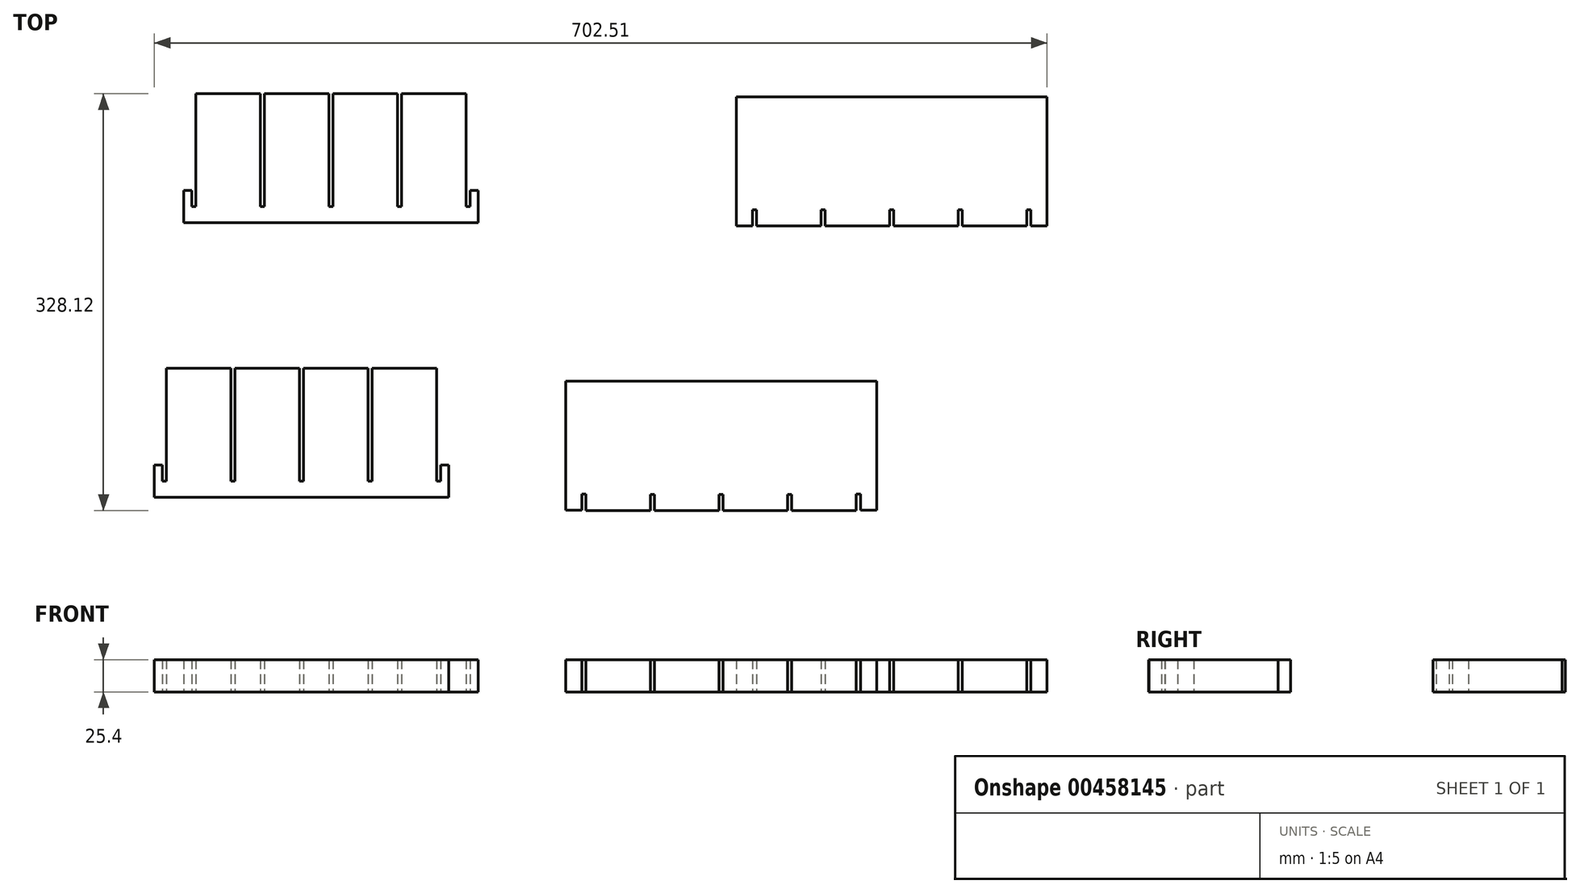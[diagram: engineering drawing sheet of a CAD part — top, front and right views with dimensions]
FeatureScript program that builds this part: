
annotation { "Feature Type Name" : "Feature", "Feature Type Description" : "" }
export const myFeature = defineFeature(function(context is Context, id is Id, definition is map)
    precondition{}
    {
        {
            var Q0;
            Q0=qCreatedBy(makeId("Top.planeOp"),FACE);
            var sketch = newSketch(context, id + "F0", { "sketchPlane" : qUnion([Q0])});
            skLineSegment(sketch, "E0", {"start": v(-688.87, 490.39) * mm, "end": v(-476.15, 490.39) * mm});
            skLineSegment(sketch, "E1", {"start": v(-476.15, 503.09) * mm, "end": v(-476.15, 591.99) * mm});
            skLineSegment(sketch, "E2", {"start": v(-476.15, 591.99) * mm, "end": v(-526.95, 591.99) * mm});
            skLineSegment(sketch, "E3", {"start": v(-526.95, 591.99) * mm, "end": v(-526.95, 503.09) * mm});
            skLineSegment(sketch, "E4", {"start": v(-530.12, 503.09) * mm, "end": v(-530.12, 591.99) * mm});
            skLineSegment(sketch, "E5", {"start": v(-530.12, 591.99) * mm, "end": v(-580.92, 591.99) * mm});
            skLineSegment(sketch, "E6", {"start": v(-580.92, 591.99) * mm, "end": v(-580.92, 503.09) * mm});
            skLineSegment(sketch, "E7", {"start": v(-584.1, 503.09) * mm, "end": v(-584.1, 591.99) * mm});
            skLineSegment(sketch, "E8", {"start": v(-584.1, 591.99) * mm, "end": v(-634.9, 591.99) * mm});
            skLineSegment(sketch, "E9", {"start": v(-634.9, 591.99) * mm, "end": v(-634.9, 503.09) * mm});
            skLineSegment(sketch, "E10", {"start": v(-638.07, 503.09) * mm, "end": v(-638.07, 591.99) * mm});
            skLineSegment(sketch, "E11", {"start": v(-638.07, 591.99) * mm, "end": v(-688.87, 591.99) * mm});
            skLineSegment(sketch, "E12", {"start": v(-688.87, 591.99) * mm, "end": v(-688.87, 503.09) * mm});
            skLineSegment(sketch, "E13", {"start": v(-584.1, 503.09) * mm, "end": v(-580.92, 503.09) * mm});
            skLineSegment(sketch, "E14", {"start": v(-530.12, 503.09) * mm, "end": v(-526.95, 503.09) * mm});
            skLineSegment(sketch, "E15", {"start": v(-638.07, 503.09) * mm, "end": v(-634.9, 503.09) * mm});
            skPoint(sketch, "E16.orphan", {"position": v(-526.95, 490.39) * mm});
            skPoint(sketch, "E17.start.orphan", {"position": v(-526.78, 490.39) * mm});
            skPoint(sketch, "E18.start.orphan", {"position": v(-580.92, 490.39) * mm});
            skPoint(sketch, "E19.start.orphan", {"position": v(-634.9, 490.39) * mm});
            skLineSegment(sketch, "E20.bottom", {"start": v(-688.87, 490.39) * mm, "end": v(-698.4, 490.39) * mm});
            skLineSegment(sketch, "E20.top", {"start": v(-688.87, 503.09) * mm, "end": v(-692.05, 503.09) * mm});
            skLineSegment(sketch, "E21.bottom", {"start": v(-476.15, 490.39) * mm, "end": v(-466.62, 490.39) * mm});
            skLineSegment(sketch, "E22", {"start": v(-247.78, 487.8) * mm, "end": v(-196.98, 487.8) * mm});
            skLineSegment(sketch, "E23", {"start": v(-247.78, 500.5) * mm, "end": v(-247.78, 487.8) * mm});
            skLineSegment(sketch, "E24", {"start": v(-143, 500.5) * mm, "end": v(-139.83, 500.5) * mm});
            skLineSegment(sketch, "E25", {"start": v(-89.03, 500.5) * mm, "end": v(-85.86, 500.5) * mm});
            skLineSegment(sketch, "E26", {"start": v(-196.98, 500.5) * mm, "end": v(-193.8, 500.5) * mm});
            skPoint(sketch, "E27.orphan", {"position": v(-85.86, 487.8) * mm});
            skPoint(sketch, "E28.start.orphan", {"position": v(-139.83, 487.8) * mm});
            skPoint(sketch, "E29.start.orphan", {"position": v(-193.8, 487.8) * mm});
            skLineSegment(sketch, "E30", {"start": v(-193.8, 500.5) * mm, "end": v(-193.8, 487.8) * mm});
            skLineSegment(sketch, "E31", {"start": v(-196.98, 500.5) * mm, "end": v(-196.98, 487.8) * mm});
            skLineSegment(sketch, "E32", {"start": v(-143, 500.5) * mm, "end": v(-143, 487.8) * mm});
            skLineSegment(sketch, "E33", {"start": v(-139.83, 500.5) * mm, "end": v(-139.83, 487.8) * mm});
            skLineSegment(sketch, "E34", {"start": v(-89.03, 500.5) * mm, "end": v(-89.03, 487.8) * mm});
            skLineSegment(sketch, "E35", {"start": v(-85.86, 500.5) * mm, "end": v(-85.86, 487.8) * mm});
            skLineSegment(sketch, "E36.trimOffspring", {"start": v(-193.8, 487.8) * mm, "end": v(-143, 487.8) * mm});
            skLineSegment(sketch, "E37.trimOffspring", {"start": v(-139.83, 487.8) * mm, "end": v(-89.03, 487.8) * mm});
            skLineSegment(sketch, "E38.trimOffspring", {"start": v(-85.86, 487.8) * mm, "end": v(-35.06, 487.8) * mm});
            skLineSegment(sketch, "E39", {"start": v(-263.66, 589.4) * mm, "end": v(-19.06, 589.4) * mm});
            skLineSegment(sketch, "E40.top", {"start": v(-247.78, 500.5) * mm, "end": v(-250.96, 500.5) * mm});
            skLineSegment(sketch, "E41.top", {"start": v(-35.06, 500.5) * mm, "end": v(-31.76, 500.5) * mm});
            skLineSegment(sketch, "E42.top", {"start": v(-31.76, 487.8) * mm, "end": v(-19.06, 487.8) * mm});
            skLineSegment(sketch, "E42.left", {"start": v(-31.76, 500.5) * mm, "end": v(-31.76, 487.8) * mm});
            skLineSegment(sketch, "E42.right", {"start": v(-19.06, 589.4) * mm, "end": v(-19.06, 487.8) * mm});
            skLineSegment(sketch, "E43.top", {"start": v(-250.96, 487.8) * mm, "end": v(-263.66, 487.8) * mm});
            skLineSegment(sketch, "E43.left", {"start": v(-250.96, 500.5) * mm, "end": v(-250.96, 487.8) * mm});
            skLineSegment(sketch, "E43.right", {"start": v(-263.66, 589.4) * mm, "end": v(-263.66, 487.8) * mm});
            skLineSegment(sketch, "E44", {"start": v(-35.06, 500.5) * mm, "end": v(-35.06, 487.8) * mm});
            skLineSegment(sketch, "E45", {"start": v(-381.95, 263.87) * mm, "end": v(-331.15, 263.87) * mm});
            skLineSegment(sketch, "E46", {"start": v(-381.95, 276.9) * mm, "end": v(-381.95, 263.87) * mm});
            skLineSegment(sketch, "E47", {"start": v(-277.18, 276.57) * mm, "end": v(-274, 276.57) * mm});
            skLineSegment(sketch, "E48", {"start": v(-223.2, 276.57) * mm, "end": v(-220.03, 276.57) * mm});
            skLineSegment(sketch, "E49", {"start": v(-331.15, 276.57) * mm, "end": v(-327.98, 276.57) * mm});
            skPoint(sketch, "E50.orphan", {"position": v(-220.03, 263.87) * mm});
            skPoint(sketch, "E51.start.orphan", {"position": v(-274, 263.87) * mm});
            skPoint(sketch, "E52.start.orphan", {"position": v(-327.98, 263.87) * mm});
            skLineSegment(sketch, "E53", {"start": v(-327.98, 276.57) * mm, "end": v(-327.98, 263.87) * mm});
            skLineSegment(sketch, "E54", {"start": v(-331.15, 276.57) * mm, "end": v(-331.15, 263.87) * mm});
            skLineSegment(sketch, "E55", {"start": v(-277.18, 276.57) * mm, "end": v(-277.18, 263.87) * mm});
            skLineSegment(sketch, "E56", {"start": v(-274, 276.57) * mm, "end": v(-274, 263.87) * mm});
            skLineSegment(sketch, "E57", {"start": v(-223.2, 276.57) * mm, "end": v(-223.2, 263.87) * mm});
            skLineSegment(sketch, "E58", {"start": v(-220.03, 276.57) * mm, "end": v(-220.03, 263.87) * mm});
            skLineSegment(sketch, "E59.trimOffspring", {"start": v(-327.98, 263.87) * mm, "end": v(-277.18, 263.87) * mm});
            skLineSegment(sketch, "E60.trimOffspring", {"start": v(-274, 263.87) * mm, "end": v(-223.2, 263.87) * mm});
            skLineSegment(sketch, "E61.trimOffspring", {"start": v(-220.03, 263.87) * mm, "end": v(-169.23, 263.87) * mm});
            skLineSegment(sketch, "E62", {"start": v(-397.83, 365.8) * mm, "end": v(-153.22, 365.8) * mm});
            skLineSegment(sketch, "E63.top", {"start": v(-381.95, 276.9) * mm, "end": v(-385.13, 276.9) * mm});
            skLineSegment(sketch, "E64.top", {"start": v(-169.23, 276.9) * mm, "end": v(-165.92, 276.9) * mm});
            skLineSegment(sketch, "E65.top", {"start": v(-165.92, 264.2) * mm, "end": v(-153.22, 264.2) * mm});
            skLineSegment(sketch, "E65.left", {"start": v(-165.92, 276.9) * mm, "end": v(-165.92, 264.2) * mm});
            skLineSegment(sketch, "E65.right", {"start": v(-153.22, 365.8) * mm, "end": v(-153.22, 264.2) * mm});
            skLineSegment(sketch, "E66.top", {"start": v(-385.13, 264.2) * mm, "end": v(-397.83, 264.2) * mm});
            skLineSegment(sketch, "E66.left", {"start": v(-385.13, 276.9) * mm, "end": v(-385.13, 264.2) * mm});
            skLineSegment(sketch, "E66.right", {"start": v(-397.83, 365.8) * mm, "end": v(-397.83, 264.2) * mm});
            skLineSegment(sketch, "E67", {"start": v(-169.23, 276.9) * mm, "end": v(-169.23, 263.87) * mm});
            skLineSegment(sketch, "E68", {"start": v(-476.15, 503.09) * mm, "end": v(-472.97, 503.09) * mm});
            skLineSegment(sketch, "E69", {"start": v(-472.97, 503.09) * mm, "end": v(-472.97, 515.79) * mm});
            skLineSegment(sketch, "E70", {"start": v(-472.97, 515.79) * mm, "end": v(-466.62, 515.79) * mm});
            skLineSegment(sketch, "E71", {"start": v(-466.62, 515.79) * mm, "end": v(-466.62, 490.39) * mm});
            skPoint(sketch, "E72", {"position": v(-582.5, 503.09) * mm});
            skLineSegment(sketch, "E73", {"start": v(-582.5, 503.09) * mm, "end": v(-582.5, 490.39) * mm});
            skLineSegment(sketch, "E74.MirrorCS", {"start": v(-698.4, 515.79) * mm, "end": v(-698.4, 490.39) * mm});
            skLineSegment(sketch, "E75.MirrorCS", {"start": v(-692.05, 515.79) * mm, "end": v(-698.4, 515.79) * mm});
            skLineSegment(sketch, "E76.MirrorCS", {"start": v(-692.05, 503.09) * mm, "end": v(-692.05, 515.79) * mm});
            skPoint(sketch, "E77.orphan", {"position": v(-701.57, 490.39) * mm});
            skLineSegment(sketch, "E78", {"start": v(-712.05, 274.14) * mm, "end": v(-499.32, 274.14) * mm});
            skLineSegment(sketch, "E79", {"start": v(-499.32, 286.84) * mm, "end": v(-499.32, 375.74) * mm});
            skLineSegment(sketch, "E80", {"start": v(-499.32, 375.74) * mm, "end": v(-550.12, 375.74) * mm});
            skLineSegment(sketch, "E81", {"start": v(-550.12, 375.74) * mm, "end": v(-550.12, 286.84) * mm});
            skLineSegment(sketch, "E82", {"start": v(-553.3, 286.84) * mm, "end": v(-553.3, 375.74) * mm});
            skLineSegment(sketch, "E83", {"start": v(-553.3, 375.74) * mm, "end": v(-604.1, 375.74) * mm});
            skLineSegment(sketch, "E84", {"start": v(-604.1, 375.74) * mm, "end": v(-604.1, 286.84) * mm});
            skLineSegment(sketch, "E85", {"start": v(-607.27, 286.84) * mm, "end": v(-607.27, 375.74) * mm});
            skLineSegment(sketch, "E86", {"start": v(-607.27, 375.74) * mm, "end": v(-658.07, 375.74) * mm});
            skLineSegment(sketch, "E87", {"start": v(-658.07, 375.74) * mm, "end": v(-658.07, 286.84) * mm});
            skLineSegment(sketch, "E88", {"start": v(-661.25, 286.84) * mm, "end": v(-661.25, 375.74) * mm});
            skLineSegment(sketch, "E89", {"start": v(-661.25, 375.74) * mm, "end": v(-712.05, 375.74) * mm});
            skLineSegment(sketch, "E90", {"start": v(-712.05, 375.74) * mm, "end": v(-712.05, 286.84) * mm});
            skLineSegment(sketch, "E91", {"start": v(-607.27, 286.84) * mm, "end": v(-604.1, 286.84) * mm});
            skLineSegment(sketch, "E92", {"start": v(-553.3, 286.84) * mm, "end": v(-550.12, 286.84) * mm});
            skLineSegment(sketch, "E93", {"start": v(-661.25, 286.84) * mm, "end": v(-658.07, 286.84) * mm});
            skPoint(sketch, "E94.orphan", {"position": v(-550.12, 274.14) * mm});
            skPoint(sketch, "E95.start.orphan", {"position": v(-549.95, 274.14) * mm});
            skPoint(sketch, "E96.start.orphan", {"position": v(-604.1, 274.14) * mm});
            skPoint(sketch, "E97.start.orphan", {"position": v(-658.07, 274.14) * mm});
            skLineSegment(sketch, "E98.bottom", {"start": v(-712.05, 274.14) * mm, "end": v(-721.57, 274.14) * mm});
            skLineSegment(sketch, "E98.top", {"start": v(-712.05, 286.84) * mm, "end": v(-715.22, 286.84) * mm});
            skLineSegment(sketch, "E99.bottom", {"start": v(-499.32, 274.14) * mm, "end": v(-489.8, 274.14) * mm});
            skLineSegment(sketch, "E100", {"start": v(-499.32, 286.84) * mm, "end": v(-496.15, 286.84) * mm});
            skLineSegment(sketch, "E101", {"start": v(-496.15, 286.84) * mm, "end": v(-496.15, 299.54) * mm});
            skLineSegment(sketch, "E102", {"start": v(-496.15, 299.54) * mm, "end": v(-489.8, 299.54) * mm});
            skLineSegment(sketch, "E103", {"start": v(-489.8, 299.54) * mm, "end": v(-489.8, 274.14) * mm});
            skPoint(sketch, "E104", {"position": v(-605.69, 286.84) * mm});
            skLineSegment(sketch, "E105", {"start": v(-605.69, 286.84) * mm, "end": v(-605.69, 274.14) * mm});
            skLineSegment(sketch, "E106.MirrorCS", {"start": v(-721.57, 299.54) * mm, "end": v(-721.57, 274.14) * mm});
            skLineSegment(sketch, "E107.MirrorCS", {"start": v(-715.22, 299.54) * mm, "end": v(-721.57, 299.54) * mm});
            skLineSegment(sketch, "E108.MirrorCS", {"start": v(-715.22, 286.84) * mm, "end": v(-715.22, 299.54) * mm});
            skPoint(sketch, "E109.orphan", {"position": v(-724.75, 274.14) * mm});
            skSolve(sketch);
        }
        {
            var Q0;
            Q0 = qSketchRegion(id + "F0", true);
            extrude(context, id + "F1", {"entities" : qUnion([Q0]), "depth" : 25.4 * mm, "offsetDistance" : 25.4 * mm});
        }
    });
